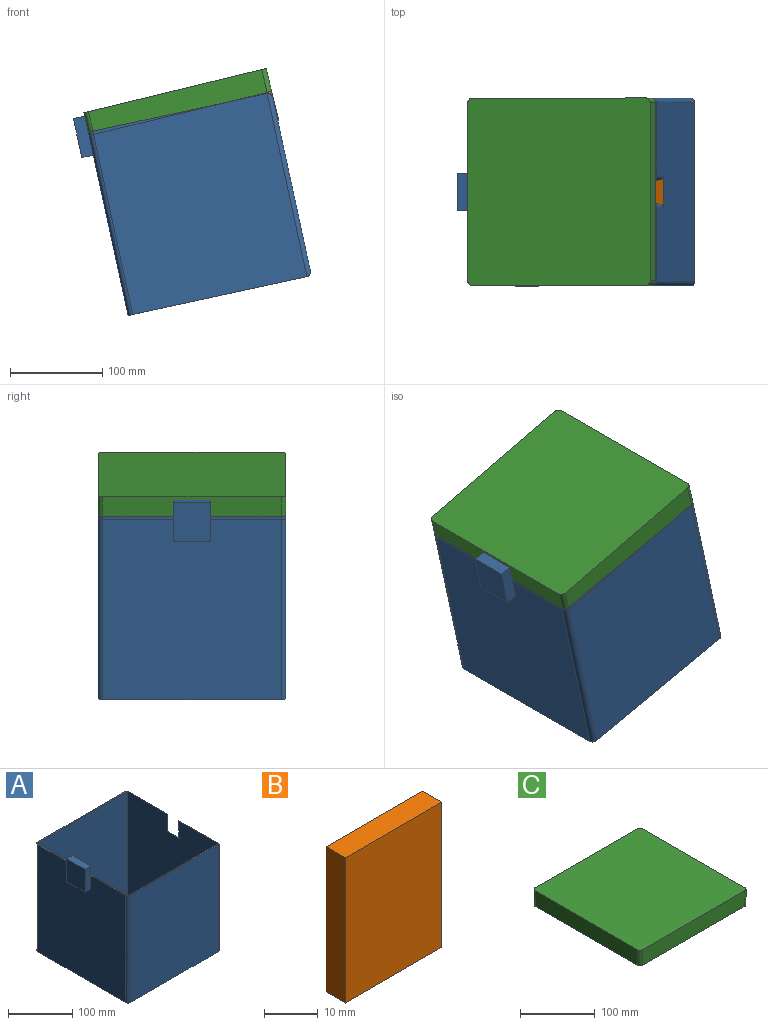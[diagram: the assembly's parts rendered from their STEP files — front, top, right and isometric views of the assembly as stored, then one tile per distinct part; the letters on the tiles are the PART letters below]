
ASSEMBLY  parts=3 mates=2
PART A: 27 faces, bbox 215.9x203.2x221 mm
  f0: plane 203.2x198.12mm, normal (0,0,1), area 1498.6mm2, adj f1,f4,f5,f6,f9,f10,f11,f18
  f1: plane 203.2x193.04mm, normal (-1,0,0), area 38193.5mm2, adj f0,f2,f19,f20,f21,f22,f23
  f2: plane 203.2x198.12mm, normal (0,0,-1), area 40246.9mm2, adj f1,f4,f5,f15,f19,f20
  f3: plane 193.04x193.04mm, normal (1,0,0), area 36158.5mm2, adj f11,f12,f13,f14,f15,f16,f17,f18
  f4: plane 203.2x193.04mm, normal (0,-1,0), area 39225.7mm2, adj f0,f2,f13,f20
  f5: plane 203.2x193.04mm, normal (0,1,0), area 39225.7mm2, adj f0,f2,f17,f19
  f6: plane 200.66x198.12mm, normal (1,0,0), area 39754.8mm2, adj f0,f7,f9,f10
  f7: plane 198.12x198.12mm, normal (0,0,1), area 39251.5mm2, adj f6,f8,f9,f10
  f8: plane 199.98x198.12mm, normal (-1,0,0), area 38798.5mm2, adj f7,f9,f10,f11,f12,f14,f16,f18
  f9: plane 200.66x198.12mm, normal (0,1,0), area 39754.2mm2, adj f0,f6,f7,f8,f11
  f10: plane 200.66x198.12mm, normal (0,-1,0), area 39754.2mm2, adj f0,f6,f7,f8,f18
  f11: cylinder r=5.08mm len=88.9mm, axis (0,1,0), area 454.5mm2, adj f0,f3,f8,f9,f12,f13
  f12: cylinder r=5.08mm len=36.74mm, axis (0,0,1), area 172mm2, adj f3,f8,f11,f14
  f13: cylinder r=5.08mm len=203.2mm, axis (0,0,-1), area 1592mm2, adj f3,f4,f11,f15
  f14: cylinder r=5.08mm len=34.2mm, axis (0,-1,0), area 156.1mm2, adj f3,f8,f12,f16
  f15: cylinder r=5.08mm len=203.2mm, axis (0,-1,0), area 1592mm2, adj f2,f3,f13,f17
  f16: cylinder r=5.08mm len=36.74mm, axis (0,0,-1), area 172mm2, adj f3,f8,f14,f18
  f17: cylinder r=5.08mm len=203.2mm, axis (0,0,1), area 1592mm2, adj f3,f5,f15,f18
  f18: cylinder r=5.08mm len=88.9mm, axis (0,1,0), area 454.5mm2, adj f0,f3,f8,f10,f16,f17
  f19: cylinder r=5.08mm len=203.2mm, axis (0,0,-1), area 1621.5mm2, adj f0,f1,f2,f5
  f20: cylinder r=5.08mm len=203.2mm, axis (0,0,1), area 1621.5mm2, adj f0,f1,f2,f4
  f21: plane 43.18x12.7mm, normal (0,1,0), area 548.4mm2, adj f1,f22,f24,f25,f26
  f22: plane 40.64x12.7mm, normal (0,0,-1), area 516.1mm2, adj f1,f21,f23,f24
  f23: plane 43.18x12.7mm, normal (0,-1,0), area 548.4mm2, adj f1,f22,f24,f25,f26
  f24: plane 43.18x40.64mm, normal (-1,0,0), area 1754.8mm2, adj f21,f22,f23,f25
  f25: plane 40.64x12.7mm, normal (0,0,1), area 516.1mm2, adj f21,f23,f24,f26
  f26: plane 40.64x17.78mm, normal (1,0,0), area 722.6mm2, adj f0,f21,f23,f25
PART B: 6 faces, bbox 25.4x5.1x33 mm
  f0: plane 33.02x5.08mm, normal (1,0,0), area 167.7mm2, adj f1,f3,f4,f5
  f1: plane 25.4x5.08mm, normal (0,0,1), area 129mm2, adj f0,f2,f4,f5
  f2: plane 33.02x5.08mm, normal (-1,0,0), area 167.7mm2, adj f1,f3,f4,f5
  f3: plane 25.4x5.08mm, normal (0,0,-1), area 129mm2, adj f0,f2,f4,f5
  f4: plane 33.02x25.4mm, normal (0,1,0), area 838.7mm2, adj f0,f1,f2,f3
  f5: plane 33.02x25.4mm, normal (0,-1,0), area 838.7mm2, adj f0,f1,f2,f3
PART C: 10 faces, bbox 203.2x203.2x25.4 mm
  f0: plane 193.04x25.4mm, normal (0,1,0), area 4903.2mm2, adj f4,f5,f6,f9
  f1: plane 193.04x25.4mm, normal (-1,0,0), area 4903.2mm2, adj f4,f5,f6,f7
  f2: plane 193.04x25.4mm, normal (0,-1,0), area 4903.2mm2, adj f4,f5,f7,f8
  f3: plane 193.04x25.4mm, normal (1,0,0), area 4903.2mm2, adj f4,f5,f8,f9
  f4: plane 203.2x203.2mm, normal (0,0,1), area 41268.1mm2, adj f0,f1,f2,f3,f6,f7,f8,f9
  f5: plane 203.2x203.2mm, normal (0,0,-1), area 41268.1mm2, adj f0,f1,f2,f3,f6,f7,f8,f9
  f6: cylinder r=5.08mm len=25.4mm, axis (0,0,1), area 202.7mm2, adj f0,f1,f4,f5
  f7: cylinder r=5.08mm len=25.4mm, axis (0,0,-1), area 202.7mm2, adj f1,f2,f4,f5
  f8: cylinder r=5.08mm len=25.4mm, axis (0,0,1), area 202.7mm2, adj f2,f3,f4,f5
  f9: cylinder r=5.08mm len=25.4mm, axis (0,0,-1), area 202.7mm2, adj f0,f3,f4,f5
PLACE A rot(axis=(0,-1,0),12.2deg) t=(165.45,0,31.61)mm fixed
PLACE B rot(axis=(-0.12,-0.12,0.99),90.8deg) t=(146.17,-101.6,130.07)mm
PLACE C rot(axis=(-0.12,-0.12,0.99),90.8deg) t=(146.25,-101.6,130.09)mm
MATE fastened C.f2 <-> B.f5  axis (0.97,0,0.24) through (244.98,-101.59,154.08)mm
MATE ball C.f0 <-> A.f26  axis (-0.97,0,-0.24) through (44.53,-101.6,118.44)mm
